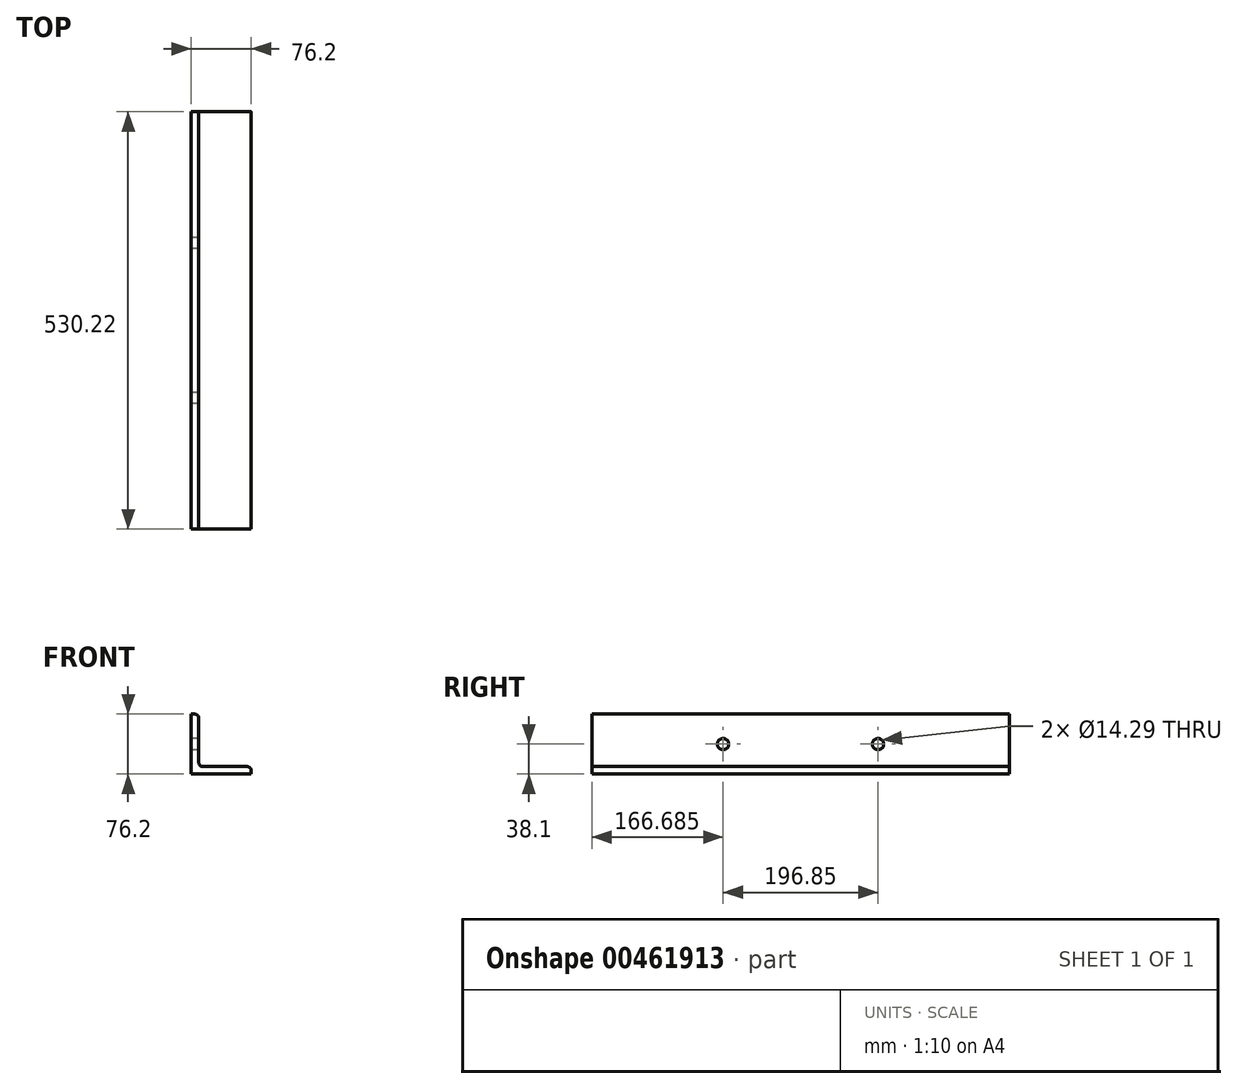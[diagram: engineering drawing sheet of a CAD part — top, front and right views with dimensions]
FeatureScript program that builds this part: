
annotation { "Feature Type Name" : "Feature", "Feature Type Description" : "" }
export const myFeature = defineFeature(function(context is Context, id is Id, definition is map)
    precondition{}
    {
        {
            var Q0;
            Q0=qCreatedBy(makeId("Front.planeOp"),FACE);
            var sketch = newSketch(context, id + "F0", { "sketchPlane" : qUnion([Q0])});
            skLineSegment(sketch, "E0", {"start": v(0, 0) * mm, "end": v(0, 76.2) * mm});
            skLineSegment(sketch, "E1", {"start": v(0, 76.2) * mm, "end": v(9.53, 76.2) * mm});
            skLineSegment(sketch, "E2", {"start": v(9.53, 76.2) * mm, "end": v(9.53, 9.52) * mm});
            skLineSegment(sketch, "E3", {"start": v(9.52, 9.52) * mm, "end": v(76.2, 9.52) * mm});
            skLineSegment(sketch, "E4", {"start": v(76.2, 9.52) * mm, "end": v(76.2, 0) * mm});
            skLineSegment(sketch, "E5", {"start": v(76.2, 0) * mm, "end": v(0, 0) * mm});
            skSolve(sketch);
        }
        {
            var Q0;
            Q0 = qSketchRegion(id + "F0", true);
            extrude(context, id + "F1", {"entities" : qUnion([Q0]), "endBound" : BoundingType.SYMMETRIC, "depth" : 530.23 * mm});
        }
        {
            var Q0;
            Q0=makeQuery(id+"F1.opExtrude","SWEPT_EDGE",EDGE,{"disambiguationData":[OSD([sQuery(id+"F0.wireOp",EDGE,"E1"),sQuery(id+"F0.wireOp",EDGE,"E2")])]});
            var Q1;
            Q1=makeQuery(id+"F1.opExtrude","SWEPT_EDGE",EDGE,{"disambiguationData":[OSD([sQuery(id+"F0.wireOp",EDGE,"E2"),sQuery(id+"F0.wireOp",EDGE,"E3")])]});
            var Q2;
            Q2=makeQuery(id+"F1.opExtrude","SWEPT_EDGE",EDGE,{"disambiguationData":[OSD([sQuery(id+"F0.wireOp",EDGE,"E3"),sQuery(id+"F0.wireOp",EDGE,"E4")])]});
            fillet(context, id + "F2", {"entities" : qUnion([Q0, Q1, Q2]), "radius" : 5.08 * mm, "tangentPropagation" : true, "allowEdgeOverflow" : false});
        }
        {
            var Q0;
            Q0=makeQuery(id+"F1.opExtrude","SWEPT_FACE",FACE,{"disambiguationData":[OSD([sQuery(id+"F0.wireOp",EDGE,"E0")])]});
            var sketch = newSketch(context, id + "F3", { "sketchPlane" : qUnion([Q0])});
            skCircle(sketch, "E6", {"center": v(-98.43, 38.1) * mm, "radius": 7.14 * mm});
            skCircle(sketch, "E7", {"center": v(98.43, 38.1) * mm, "radius": 7.14 * mm});
            skSolve(sketch);
        }
        {
            var Q0;
            Q0 = qSketchRegion(id + "F3", true);
            extrude(context, id + "F4", {"entities" : qUnion([Q0]), "operationType" : NewBodyOperationType.REMOVE, "oppositeDirection" : true, "depth" : 25.4 * mm});
        }
    });
